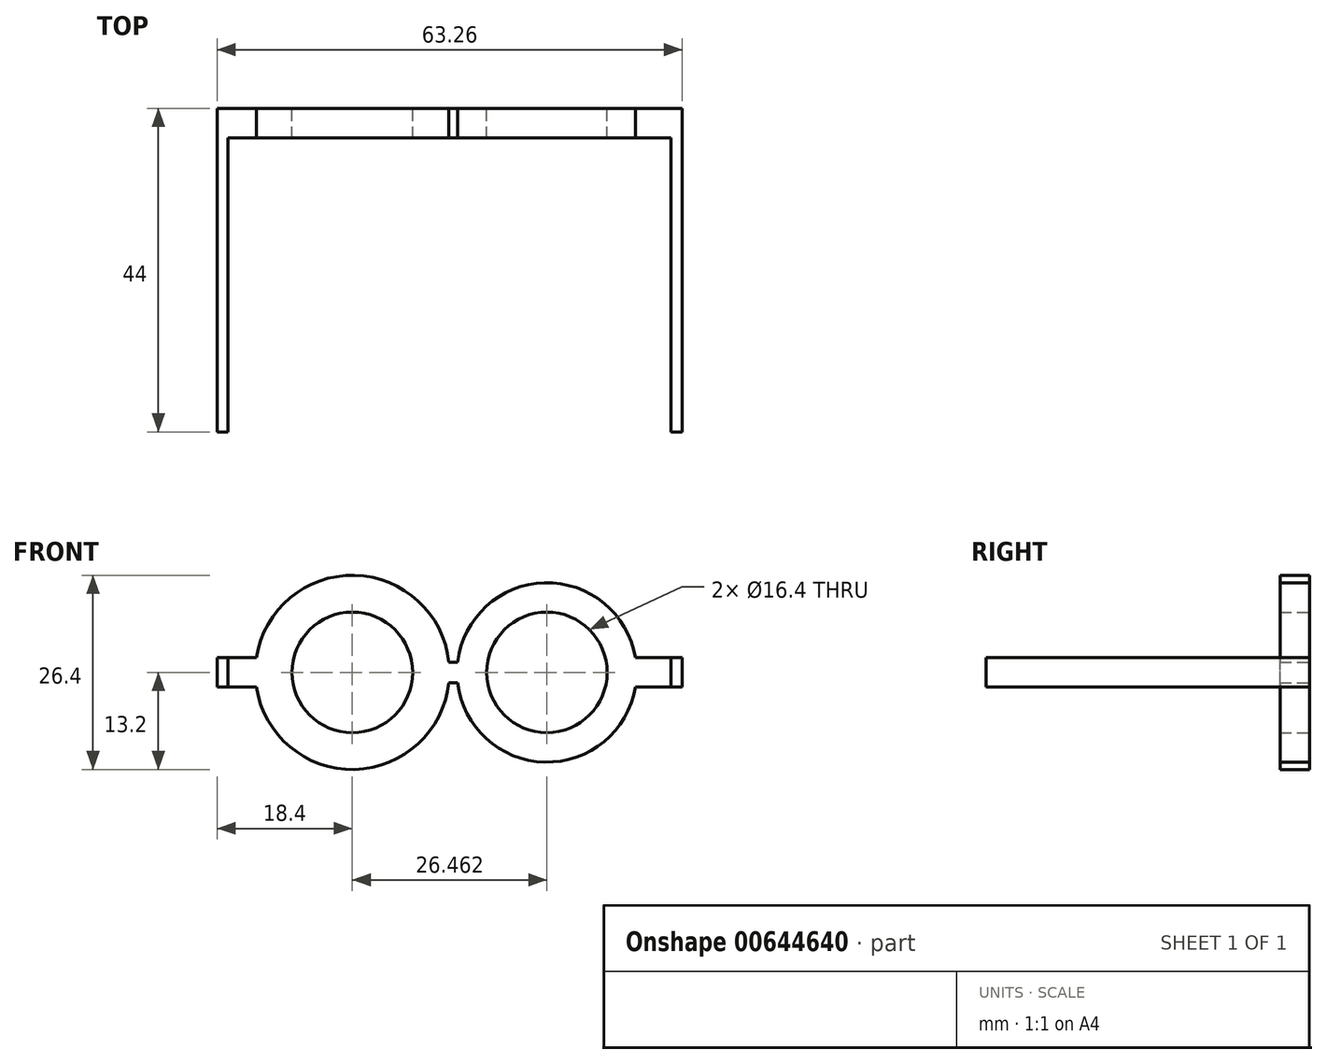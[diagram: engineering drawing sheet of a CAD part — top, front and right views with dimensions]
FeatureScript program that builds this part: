
annotation { "Feature Type Name" : "Feature", "Feature Type Description" : "" }
export const myFeature = defineFeature(function(context is Context, id is Id, definition is map)
    precondition{}
    {
        {
            var Q0;
            Q0=qCreatedBy(makeId("Front.planeOp"),FACE);
            var sketch = newSketch(context, id + "F0", { "sketchPlane" : qUnion([Q0])});
            skCircle(sketch, "E0", {"center": v(0, 0) * mm, "radius": 8.2 * mm});
            skArc(sketch, "E1.0", {"start": v(-13.05, -2) * mm, "mid": v(0.31, -13.2) * mm, "end": v(13.13, -1.38) * mm});
            skCircle(sketch, "E2", {"center": v(26.46, 0) * mm, "radius": 8.2 * mm});
            skArc(sketch, "E3.0", {"start": v(38.5, 2) * mm, "mid": v(26.15, 12.2) * mm, "end": v(14.34, 1.38) * mm});
            skLineSegment(sketch, "E4.bottom", {"start": v(14.34, 1.38) * mm, "end": v(13.13, 1.38) * mm});
            skLineSegment(sketch, "E4.top", {"start": v(14.34, -1.38) * mm, "end": v(13.13, -1.38) * mm});
            skPoint(sketch, "E4.middle", {"position": v(13.2, 0) * mm});
            skLineSegment(sketch, "E5.right", {"start": v(44.86, 2) * mm, "end": v(44.86, -2) * mm});
            skPoint(sketch, "E5.middle", {"position": v(35.66, 0) * mm});
            skLineSegment(sketch, "E6.bottom", {"start": v(-18.4, 2) * mm, "end": v(-13.05, 2) * mm});
            skLineSegment(sketch, "E6.top", {"start": v(-18.4, -2) * mm, "end": v(-13.05, -2) * mm});
            skLineSegment(sketch, "E6.left", {"start": v(-18.4, 2) * mm, "end": v(-18.4, -2) * mm});
            skPoint(sketch, "E6.middle", {"position": v(-9.2, 0) * mm});
            skLineSegment(sketch, "E7.trimOffspring", {"start": v(38.5, -2) * mm, "end": v(44.86, -2) * mm});
            skLineSegment(sketch, "E8.trimOffspring", {"start": v(38.5, 2) * mm, "end": v(44.86, 2) * mm});
            skPoint(sketch, "E5.left.start.orphan", {"position": v(26.46, 2) * mm});
            skPoint(sketch, "E5.top.start.orphan", {"position": v(26.46, -2) * mm});
            skPoint(sketch, "E9.orphan", {"position": v(0, 2) * mm});
            skPoint(sketch, "E6.right.end.orphan", {"position": v(0, -2) * mm});
            skPoint(sketch, "E4.right.start.orphan", {"position": v(9.4, 1.38) * mm});
            skPoint(sketch, "E10.orphan", {"position": v(9.4, -1.38) * mm});
            skPoint(sketch, "E4.left.end.orphan", {"position": v(17, -1.38) * mm});
            skPoint(sketch, "E11.orphan", {"position": v(17, 1.38) * mm});
            skArc(sketch, "E12.trimOffspring", {"start": v(14.34, -1.38) * mm, "mid": v(26.15, -12.2) * mm, "end": v(38.5, -2) * mm});
            skArc(sketch, "E13.trimOffspring", {"start": v(13.13, 1.38) * mm, "mid": v(0.31, 13.2) * mm, "end": v(-13.05, 2) * mm});
            skSolve(sketch);
        }
        {
            var Q0;
            Q0 = qSketchRegion(id + "F0", true);
            extrude(context, id + "F1", {"entities" : qUnion([Q0]), "depth" : 4 * mm, "offsetDistance" : 25 * mm});
        }
        {
            var Q0;
            Q0=makeQuery(id+"F1.opExtrude","CAP_FACE",FACE,{"disambiguationData":[OSD([sQuery(id+"F0.wireOp",EDGE,"E0"),sQuery(id+"F0.wireOp",EDGE,"E1.0"),sQuery(id+"F0.wireOp",EDGE,"E2"),sQuery(id+"F0.wireOp",EDGE,"E3.0"),sQuery(id+"F0.wireOp",EDGE,"E4.bottom"),sQuery(id+"F0.wireOp",EDGE,"E4.top"),sQuery(id+"F0.wireOp",EDGE,"E5.right"),sQuery(id+"F0.wireOp",EDGE,"E6.bottom"),sQuery(id+"F0.wireOp",EDGE,"E6.top"),sQuery(id+"F0.wireOp",EDGE,"E6.left"),sQuery(id+"F0.wireOp",EDGE,"E7.trimOffspring"),sQuery(id+"F0.wireOp",EDGE,"E8.trimOffspring"),sQuery(id+"F0.wireOp",EDGE,"E12.trimOffspring"),sQuery(id+"F0.wireOp",EDGE,"E13.trimOffspring")])],"isStart":false});
            var sketch = newSketch(context, id + "F2", { "sketchPlane" : qUnion([Q0])});
            skLineSegment(sketch, "E14.bottom", {"start": v(43.36, 2) * mm, "end": v(44.86, 2) * mm});
            skLineSegment(sketch, "E14.top", {"start": v(43.36, -2) * mm, "end": v(44.86, -2) * mm});
            skLineSegment(sketch, "E14.left", {"start": v(43.36, 2) * mm, "end": v(43.36, -2) * mm});
            skLineSegment(sketch, "E14.right", {"start": v(44.86, 2) * mm, "end": v(44.86, -2) * mm});
            skLineSegment(sketch, "E15.bottom", {"start": v(-16.9, -2) * mm, "end": v(-18.4, -2) * mm});
            skLineSegment(sketch, "E15.top", {"start": v(-16.9, 2) * mm, "end": v(-18.4, 2) * mm});
            skLineSegment(sketch, "E15.left", {"start": v(-16.9, -2) * mm, "end": v(-16.9, 2) * mm});
            skLineSegment(sketch, "E15.right", {"start": v(-18.4, -2) * mm, "end": v(-18.4, 2) * mm});
            skSolve(sketch);
        }
        {
            var Q0;
            Q0=makeQuery(id+"F2.imprint","IMPRINT",FACE,{"disambiguationData":[TD([[makeQuery(id+"F2.imprint","IMPRINT",EDGE,{"derivedFrom":sQuery(id+"F2.wireOp",EDGE,"E15.bottom")}),1.0]])]});
            var Q1;
            Q1=makeQuery(id+"F2.imprint","IMPRINT",FACE,{"disambiguationData":[TD([[makeQuery(id+"F2.imprint","IMPRINT",EDGE,{"derivedFrom":sQuery(id+"F2.wireOp",EDGE,"E14.bottom")}),-1.0]])]});
            extrude(context, id + "F3", {"entities" : qUnion([Q0, Q1]), "operationType" : NewBodyOperationType.ADD, "depth" : 40 * mm, "offsetDistance" : 25 * mm});
        }
    });
